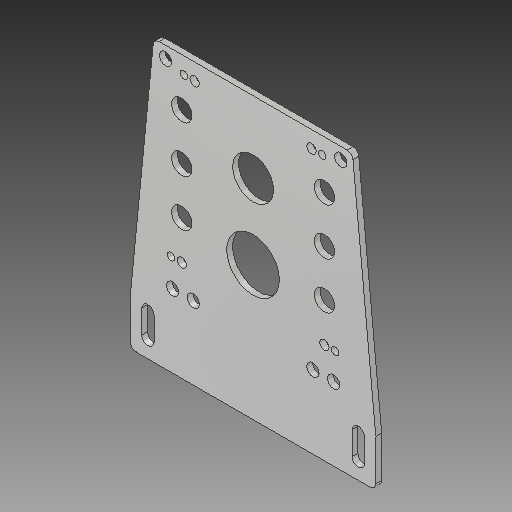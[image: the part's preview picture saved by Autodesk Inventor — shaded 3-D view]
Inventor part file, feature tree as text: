
AUTODESK INVENTOR PART (.ipt)
format: ipt  version: 2018 (Build 220112000, 112)  size: 202,752 bytes
history: native  units: in
note: dims shown in document units (in); Inventor stores cm internally (conversion verified against a paired STEP export)
features: move_body x2, direct_edit x1, fillet x1
ambient origin geometry x8: Origin, YZ Plane, XZ Plane, XY Plane, X Axis, Y Axis, Z Axis, Center Point
bodies: Solid1 (feature_tree)
feature tree (4):
  direct_edit  "Direct Edit1"
  fillet  "Fillet5"  [1 undecoded]
  move_body  "Move1"
  move_body  "Move2"
note: 1 required parameter value undecoded (feature->parameter linkage not recoverable at this tier; creation-order binding heuristic only, values carry confidence <= 0.55)
